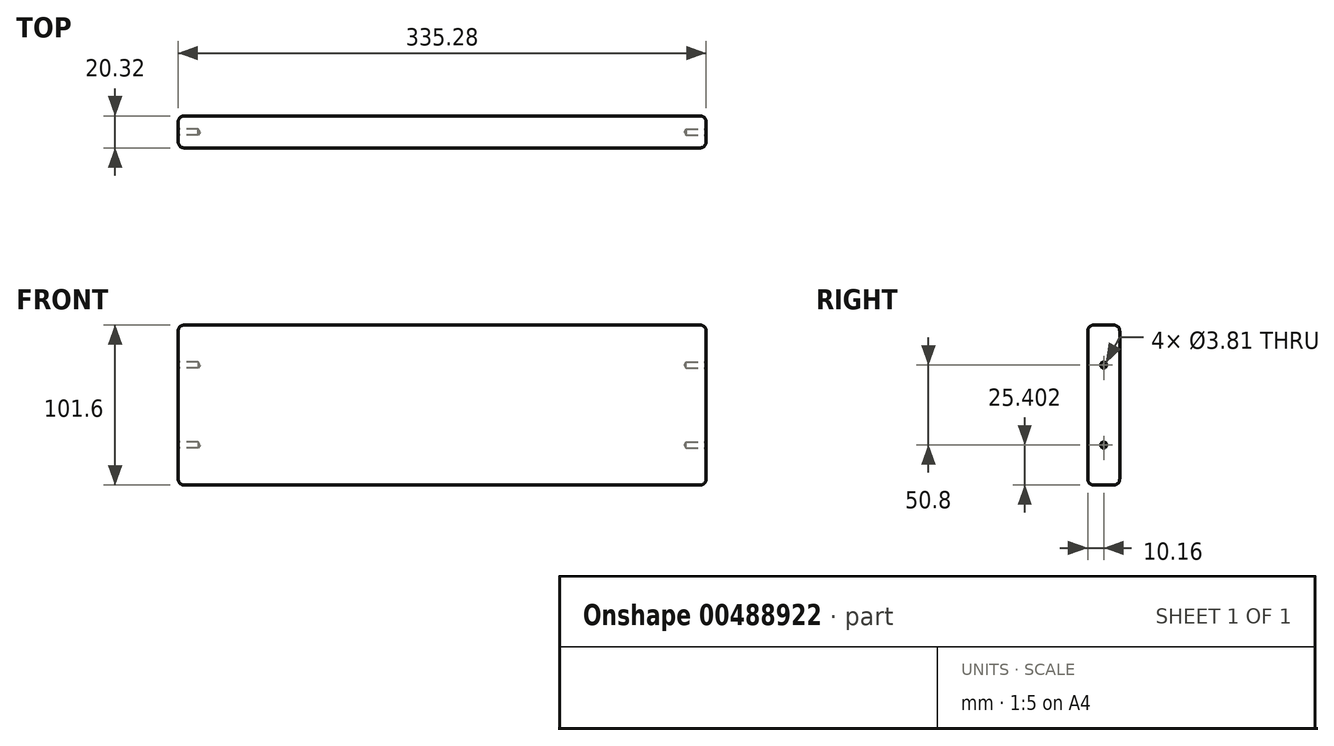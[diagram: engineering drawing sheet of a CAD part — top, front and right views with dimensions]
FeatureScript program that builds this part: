
annotation { "Feature Type Name" : "Feature", "Feature Type Description" : "" }
export const myFeature = defineFeature(function(context is Context, id is Id, definition is map)
    precondition{}
    {
        {
            var Q0;
            Q0=qCreatedBy(makeId("Front.planeOp"),FACE);
            var sketch = newSketch(context, id + "F0", { "sketchPlane" : qUnion([Q0])});
            skLineSegment(sketch, "E0.bottom", {"start": v(-209.73, 83.5) * mm, "end": v(125.55, 83.5) * mm});
            skLineSegment(sketch, "E0.top", {"start": v(-209.73, -18.1) * mm, "end": v(125.55, -18.1) * mm});
            skLineSegment(sketch, "E0.left", {"start": v(-209.73, 83.5) * mm, "end": v(-209.73, -18.1) * mm});
            skLineSegment(sketch, "E0.right", {"start": v(125.55, 83.5) * mm, "end": v(125.55, -18.1) * mm});
            skSolve(sketch);
        }
        {
            var Q0;
            Q0 = qSketchRegion(id + "F0", true);
            extrude(context, id + "F1", {"entities" : qUnion([Q0]), "endBound" : BoundingType.SYMMETRIC, "depth" : 20.32 * mm});
        }
        {
            var Q0;
            Q0=makeQuery(id+"F1.opExtrude","CAP_FACE",FACE,{"disambiguationData":[OSD([sQuery(id+"F0.wireOp",EDGE,"E0.bottom"),sQuery(id+"F0.wireOp",EDGE,"E0.top"),sQuery(id+"F0.wireOp",EDGE,"E0.left"),sQuery(id+"F0.wireOp",EDGE,"E0.right")])],"isStart":false});
            var Q1;
            Q1=makeQuery(id+"F1.opExtrude","CAP_EDGE",EDGE,{"disambiguationData":[OSD([sQuery(id+"F0.wireOp",EDGE,"E0.top")])],"isStart":true});
            var Q2;
            Q2=makeQuery(id+"F1.opExtrude","CAP_EDGE",EDGE,{"disambiguationData":[OSD([sQuery(id+"F0.wireOp",EDGE,"E0.top")])],"isStart":false});
            var Q3;
            Q3=makeQuery(id+"F1.opExtrude","CAP_FACE",FACE,{"disambiguationData":[OSD([sQuery(id+"F0.wireOp",EDGE,"E0.bottom"),sQuery(id+"F0.wireOp",EDGE,"E0.top"),sQuery(id+"F0.wireOp",EDGE,"E0.left"),sQuery(id+"F0.wireOp",EDGE,"E0.right")])],"isStart":true});
            var Q4;
            Q4=makeQuery(id+"F1.opExtrude","SWEPT_FACE",FACE,{"disambiguationData":[OSD([sQuery(id+"F0.wireOp",EDGE,"E0.right")])]});
            var Q5;
            Q5=makeQuery(id+"F1.opExtrude","SWEPT_FACE",FACE,{"disambiguationData":[OSD([sQuery(id+"F0.wireOp",EDGE,"E0.bottom")])]});
            var Q6;
            Q6=makeQuery(id+"F1.opExtrude","SWEPT_EDGE",EDGE,{"disambiguationData":[OSD([sQuery(id+"F0.wireOp",EDGE,"E0.top"),sQuery(id+"F0.wireOp",EDGE,"E0.right")])]});
            var Q7;
            Q7=makeQuery(id+"F1.opExtrude","CAP_EDGE",EDGE,{"disambiguationData":[OSD([sQuery(id+"F0.wireOp",EDGE,"E0.right")])],"isStart":true});
            var Q8;
            Q8=makeQuery(id+"F1.opExtrude","CAP_EDGE",EDGE,{"disambiguationData":[OSD([sQuery(id+"F0.wireOp",EDGE,"E0.right")])],"isStart":false});
            fillet(context, id + "F2", {"entities" : qUnion([Q0, Q1, Q2, Q3, Q4, Q5, Q6, Q7, Q8]), "radius" : 3.8 * mm, "tangentPropagation" : true, "allowEdgeOverflow" : false});
        }
        {
            var Q0;
            Q0=makeQuery(id+"F1.opExtrude","SWEPT_FACE",FACE,{"disambiguationData":[OSD([sQuery(id+"F0.wireOp",EDGE,"E0.right")])]});
            var sketch = newSketch(context, id + "F3", { "sketchPlane" : qUnion([Q0])});
            skLineSegment(sketch, "E1", {"start": v(0, 79.68) * mm, "end": v(0, 58.1) * mm});
            skPoint(sketch, "E1.endSnap0", {"position": v(0, -14.3) * mm});
            skLineSegment(sketch, "E2", {"start": v(0, 58.1) * mm, "end": v(0, 7.3) * mm});
            skLineSegment(sketch, "E3", {"start": v(0, 7.3) * mm, "end": v(0, -14.3) * mm});
            skSolve(sketch);
        }
        {
            var Q0;
            Q0=sQuery(id+"F3.wireOp",VERTEX,"E2.start");
            var Q1;
            Q1=makeQuery(id+"F1.opExtrude","SWEPT_BODY",BODY,{"disambiguationData":[OSD([sQuery(id+"F0.wireOp",EDGE,"E0.bottom"),sQuery(id+"F0.wireOp",EDGE,"E0.top"),sQuery(id+"F0.wireOp",EDGE,"E0.left"),sQuery(id+"F0.wireOp",EDGE,"E0.right")])]});
            hole(context, id + "F4", {"style" : HoleStyle.SIMPLE, "endStyle" : HoleEndStyle.BLIND, "holeDiameter" : 3.8 * mm, "holeDepth" : 12.7 * mm, "isTappedThrough" : true, "tappedDepth" : 12.7 * mm, "tapClearance" : 3, "locations" : qUnion([Q0]), "scope" : qUnion([Q1])});
        }
        {
            var Q0;
            Q0=sQuery(id+"F3.wireOp",VERTEX,"E3.start");
            var Q1;
            Q1=makeQuery(id+"F1.opExtrude","SWEPT_BODY",BODY,{"disambiguationData":[OSD([sQuery(id+"F0.wireOp",EDGE,"E0.bottom"),sQuery(id+"F0.wireOp",EDGE,"E0.top"),sQuery(id+"F0.wireOp",EDGE,"E0.left"),sQuery(id+"F0.wireOp",EDGE,"E0.right")])]});
            hole(context, id + "F5", {"style" : HoleStyle.SIMPLE, "endStyle" : HoleEndStyle.BLIND, "holeDiameter" : 3.8 * mm, "holeDepth" : 12.7 * mm, "isTappedThrough" : true, "tappedDepth" : 12.7 * mm, "tapClearance" : 3, "locations" : qUnion([Q0]), "scope" : qUnion([Q1])});
        }
        {
            var Q0;
            Q0=makeQuery(id+"F1.opExtrude","SWEPT_EDGE",EDGE,{"disambiguationData":[OSD([sQuery(id+"F0.wireOp",EDGE,"E0.top"),sQuery(id+"F0.wireOp",EDGE,"E0.left")])]});
            fillet(context, id + "F6", {"entities" : qUnion([Q0]), "radius" : 3.8 * mm, "tangentPropagation" : true, "allowEdgeOverflow" : false});
        }
        {
            var Q0;
            Q0=makeQuery(id+"F1.opExtrude","SWEPT_FACE",FACE,{"disambiguationData":[OSD([sQuery(id+"F0.wireOp",EDGE,"E0.left")])]});
            var sketch = newSketch(context, id + "F7", { "sketchPlane" : qUnion([Q0])});
            skLineSegment(sketch, "E4", {"start": v(0, 79.68) * mm, "end": v(0, 58.1) * mm});
            skPoint(sketch, "E4.endSnap0", {"position": v(0, 79.68) * mm});
            skLineSegment(sketch, "E5", {"start": v(0, 58.1) * mm, "end": v(0, 7.3) * mm});
            skLineSegment(sketch, "E6", {"start": v(0, 7.3) * mm, "end": v(0, -14.3) * mm});
            skSolve(sketch);
        }
        {
            var Q0;
            Q0=sQuery(id+"F7.wireOp",VERTEX,"E5.start");
            var Q1;
            Q1=makeQuery(id+"F1.opExtrude","SWEPT_BODY",BODY,{"disambiguationData":[OSD([sQuery(id+"F0.wireOp",EDGE,"E0.bottom"),sQuery(id+"F0.wireOp",EDGE,"E0.top"),sQuery(id+"F0.wireOp",EDGE,"E0.left"),sQuery(id+"F0.wireOp",EDGE,"E0.right")])]});
            hole(context, id + "F8", {"style" : HoleStyle.SIMPLE, "endStyle" : HoleEndStyle.BLIND, "holeDiameter" : 3.8 * mm, "holeDepth" : 12.7 * mm, "isTappedThrough" : true, "tappedDepth" : 12.7 * mm, "tapClearance" : 3, "locations" : qUnion([Q0]), "scope" : qUnion([Q1])});
        }
        {
            var Q0;
            Q0=sQuery(id+"F7.wireOp",VERTEX,"E6.start");
            var Q1;
            Q1=makeQuery(id+"F1.opExtrude","SWEPT_BODY",BODY,{"disambiguationData":[OSD([sQuery(id+"F0.wireOp",EDGE,"E0.bottom"),sQuery(id+"F0.wireOp",EDGE,"E0.top"),sQuery(id+"F0.wireOp",EDGE,"E0.left"),sQuery(id+"F0.wireOp",EDGE,"E0.right")])]});
            hole(context, id + "F9", {"style" : HoleStyle.SIMPLE, "endStyle" : HoleEndStyle.BLIND, "holeDiameter" : 3.8 * mm, "holeDepth" : 12.7 * mm, "isTappedThrough" : true, "tappedDepth" : 12.7 * mm, "tapClearance" : 3, "locations" : qUnion([Q0]), "scope" : qUnion([Q1])});
        }
    });
